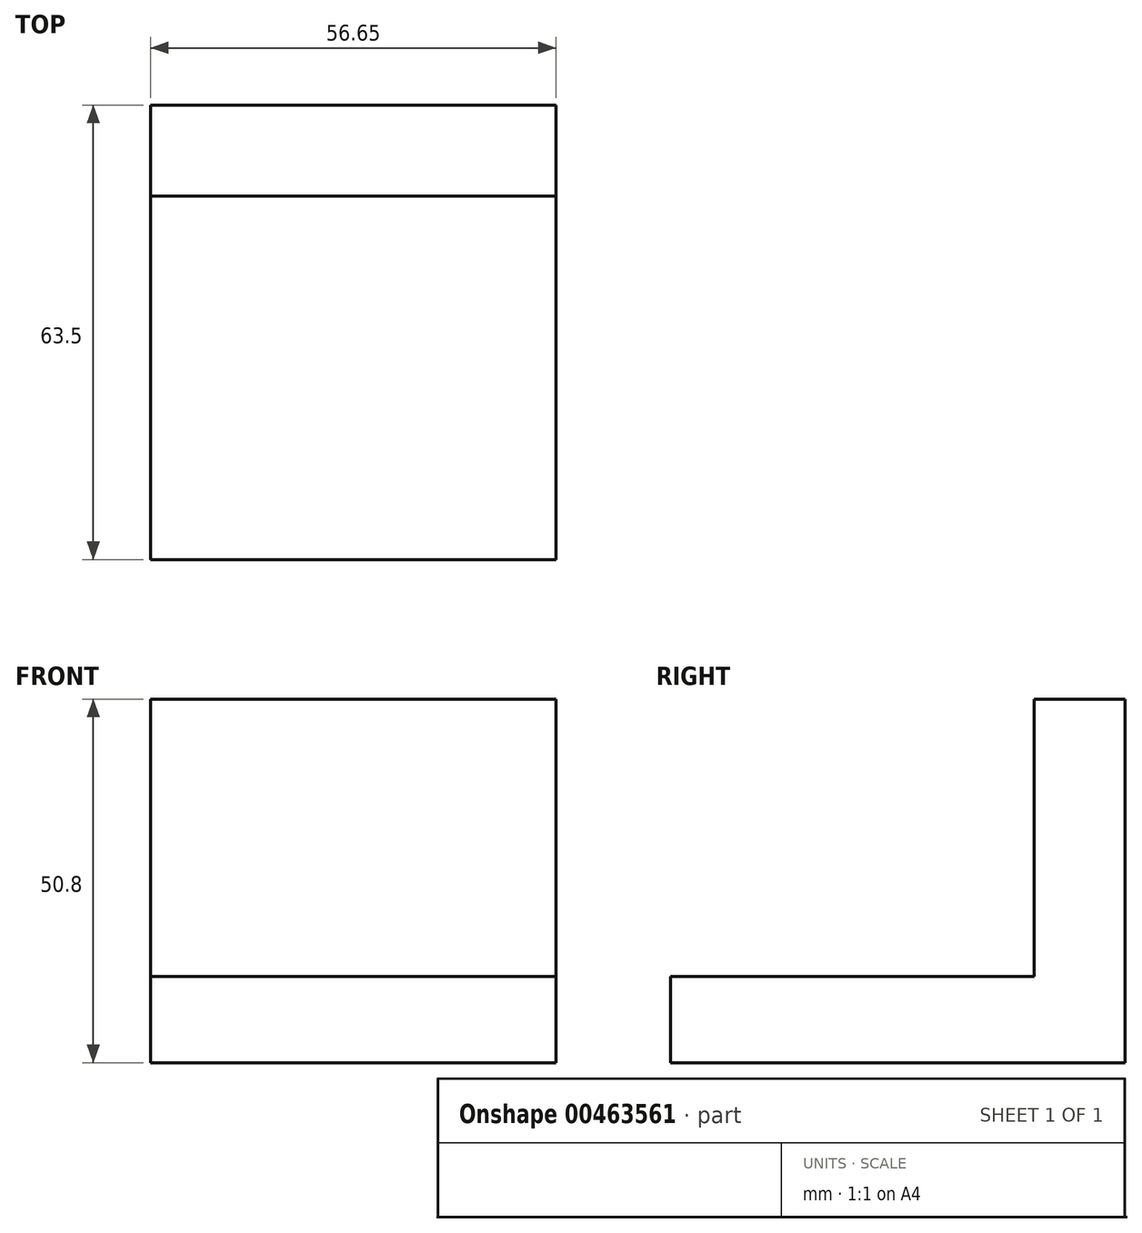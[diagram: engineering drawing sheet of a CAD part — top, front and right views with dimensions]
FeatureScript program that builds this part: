
annotation { "Feature Type Name" : "Feature", "Feature Type Description" : "" }
export const myFeature = defineFeature(function(context is Context, id is Id, definition is map)
    precondition{}
    {
        {
            var Q0;
            Q0=qCreatedBy(makeId("Front.planeOp"),FACE);
            var sketch = newSketch(context, id + "F0", { "sketchPlane" : qUnion([Q0])});
            skLineSegment(sketch, "E0.bottom", {"start": v(-27.86, 26.7) * mm, "end": v(28.79, 26.7) * mm});
            skLineSegment(sketch, "E0.top", {"start": v(-27.86, -24.1) * mm, "end": v(28.79, -24.1) * mm});
            skLineSegment(sketch, "E0.left", {"start": v(-27.86, 26.7) * mm, "end": v(-27.86, -24.1) * mm});
            skLineSegment(sketch, "E0.right", {"start": v(28.79, 26.7) * mm, "end": v(28.79, -24.1) * mm});
            skSolve(sketch);
        }
        {
            var Q0;
            Q0 = qSketchRegion(id + "F0", true);
            extrude(context, id + "F1", {"entities" : qUnion([Q0]), "depth" : 12.7 * mm});
        }
        {
            var Q0;
            Q0=makeQuery(id+"F1.opExtrude","CAP_FACE",FACE,{"disambiguationData":[OSD([sQuery(id+"F0.wireOp",EDGE,"E0.bottom"),sQuery(id+"F0.wireOp",EDGE,"E0.top"),sQuery(id+"F0.wireOp",EDGE,"E0.left"),sQuery(id+"F0.wireOp",EDGE,"E0.right")])],"isStart":false});
            var sketch = newSketch(context, id + "F2", { "sketchPlane" : qUnion([Q0])});
            skLineSegment(sketch, "E1", {"start": v(-27.86, -12.08) * mm, "end": v(28.79, -12.08) * mm});
            skSolve(sketch);
        }
        {
            var Q0;
            Q0 = qSketchRegion(id + "F2", true);
            var Q1;
            {var subQ0=sQuery(id+"F2.wireOp",EDGE,"E1");Q1=makeQuery(id+"F2.imprint","IMPRINT",FACE,{"disambiguationData":[TD([[makeQuery(id+"F2.imprint","IMPRINT",EDGE,{"derivedFrom":subQ0}),-1.0]])]});}
            extrude(context, id + "F3", {"entities" : qUnion([Q0, Q1]), "operationType" : NewBodyOperationType.ADD, "depth" : 50.8 * mm});
        }
    });
